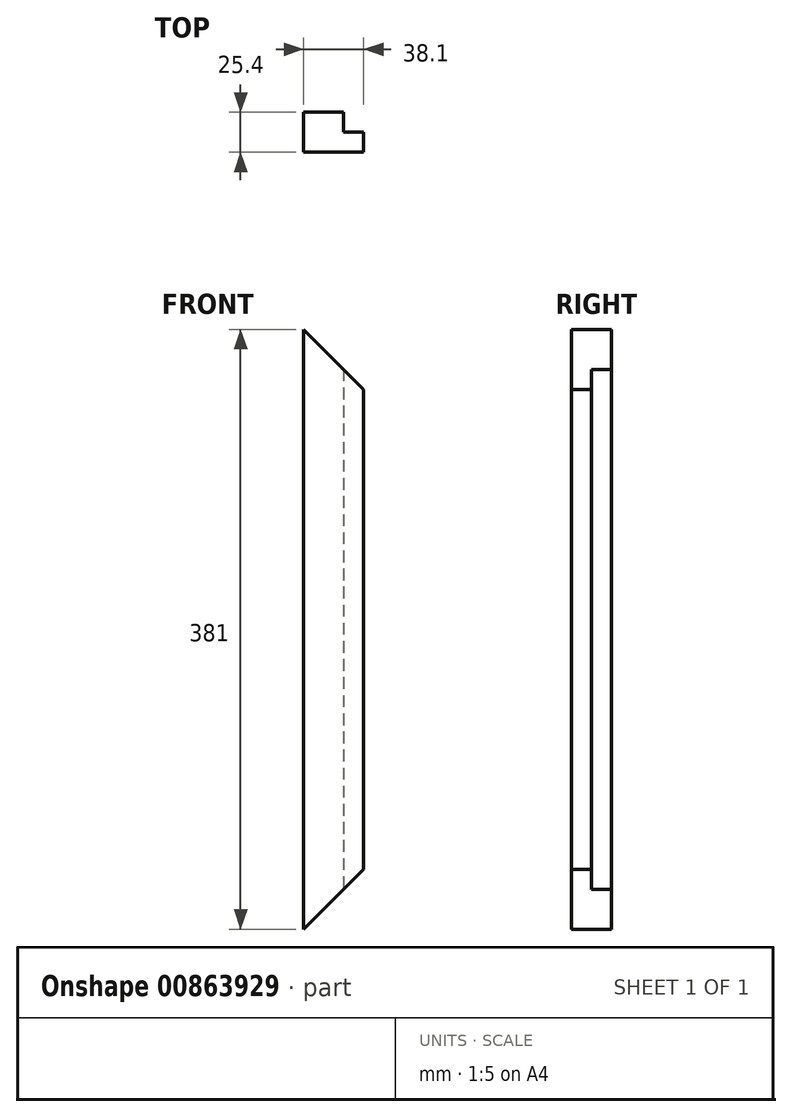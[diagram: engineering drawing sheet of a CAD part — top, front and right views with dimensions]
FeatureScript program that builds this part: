
annotation { "Feature Type Name" : "Feature", "Feature Type Description" : "" }
export const myFeature = defineFeature(function(context is Context, id is Id, definition is map)
    precondition{}
    {
        {
            var Q0;
            Q0=qCreatedBy(makeId("Front.planeOp"),FACE);
            var sketch = newSketch(context, id + "F0", { "sketchPlane" : qUnion([Q0])});
            skLineSegment(sketch, "E0", {"start": v(0, 381) * mm, "end": v(0, 0) * mm});
            skLineSegment(sketch, "E1", {"start": v(0, 0) * mm, "end": v(38.1, 38.1) * mm});
            skLineSegment(sketch, "E2", {"start": v(38.1, 38.1) * mm, "end": v(38.1, 342.9) * mm});
            skLineSegment(sketch, "E3", {"start": v(38.1, 342.9) * mm, "end": v(0, 381) * mm});
            skSolve(sketch);
        }
        {
            var Q0;
            Q0=makeQuery(id+"F0.imprint","IMPRINT",FACE,{"disambiguationData":[TD([[makeQuery(id+"F0.imprint","IMPRINT",EDGE,{"derivedFrom":sQuery(id+"F0.wireOp",EDGE,"E0")}),1.0]])]});
            extrude(context, id + "F1", {"entities" : qUnion([Q0]), "depth" : 25.4 * mm, "offsetDistance" : 25.4 * mm});
        }
        {
            var Q0;
            Q0=makeQuery(id+"F1.opExtrude","CAP_FACE",FACE,{"disambiguationData":[OSD([sQuery(id+"F0.wireOp",EDGE,"E0"),sQuery(id+"F0.wireOp",EDGE,"E1"),sQuery(id+"F0.wireOp",EDGE,"E2"),sQuery(id+"F0.wireOp",EDGE,"E3")])],"isStart":true});
            var sketch = newSketch(context, id + "F2", { "sketchPlane" : qUnion([Q0])});
            skLineSegment(sketch, "E4", {"start": v(-25.4, 355.6) * mm, "end": v(-25.4, 25.4) * mm});
            skSolve(sketch);
        }
        {
            var Q0;
            {var subQ0=sQuery(id+"F2.wireOp",EDGE,"E4");Q0=makeQuery(id+"F2.imprint","IMPRINT",FACE,{"disambiguationData":[TD([[makeQuery(id+"F2.imprint","IMPRINT",EDGE,{"derivedFrom":subQ0}),-1.0]])]});}
            extrude(context, id + "F3", {"entities" : qUnion([Q0]), "operationType" : NewBodyOperationType.REMOVE, "oppositeDirection" : true, "depth" : 12.7 * mm, "offsetDistance" : 25.4 * mm});
        }
    });
